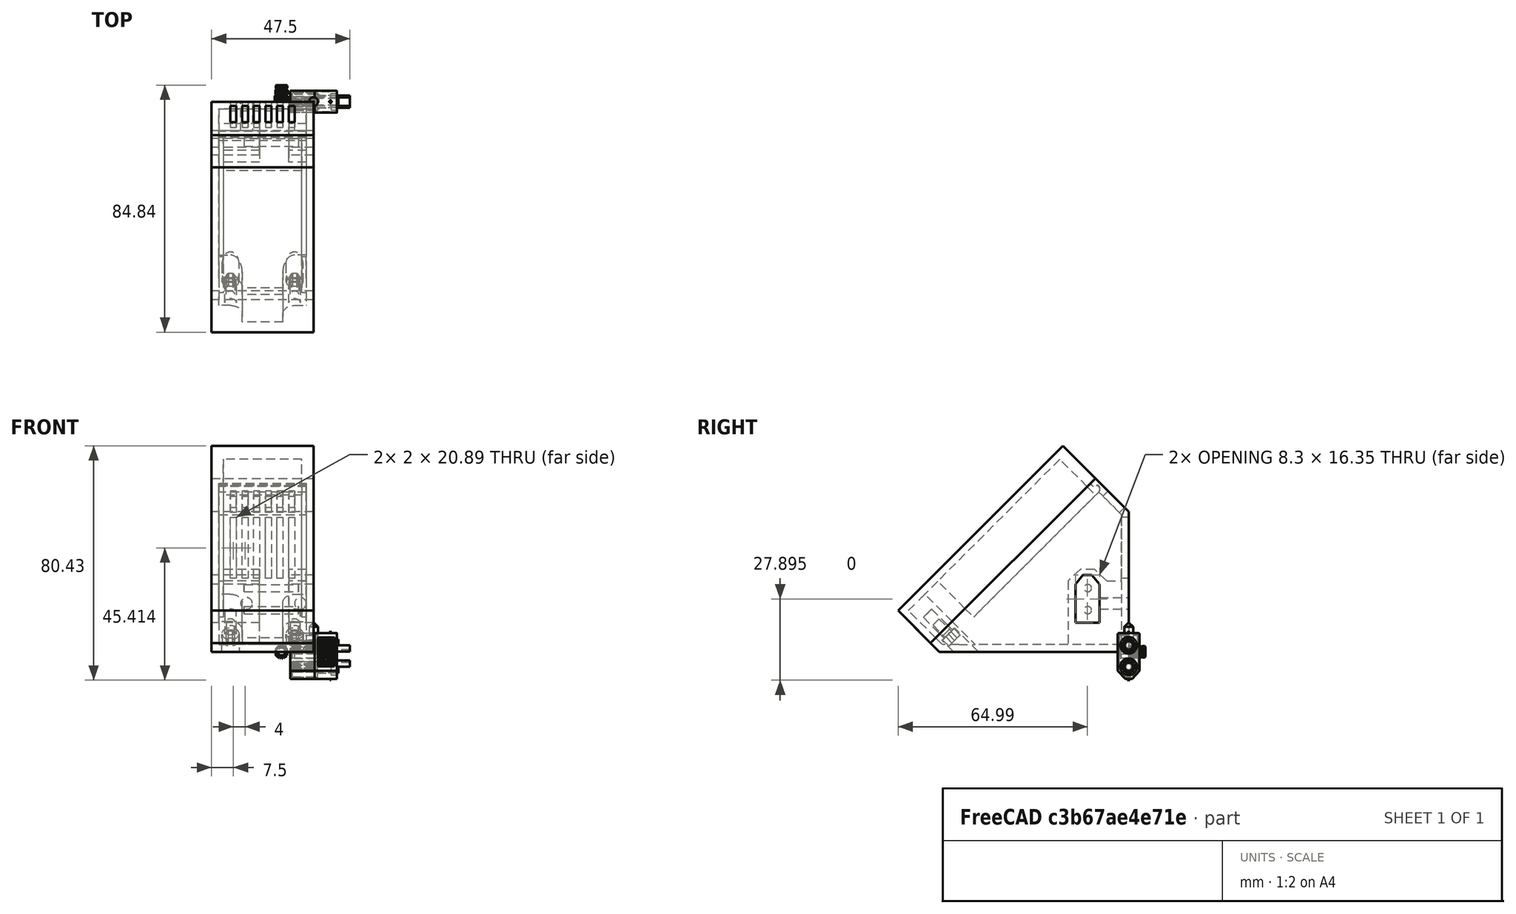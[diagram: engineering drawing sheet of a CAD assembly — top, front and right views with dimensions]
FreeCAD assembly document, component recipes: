
FREECAD ASSEMBLY — COMPONENT RECIPES ("alimMultiple_001_SurBase35mm_009.1")

This assembly document has 8 components, labeled P0..P7 below (a component is one placed body or linked part). 6 of them carry a construction recipe — the FreeCAD feature program that regenerates the part from scratch, quoted from this document or its linked companion documents; the rest are supplied as boundary geometry only. No exploded tour is included for this assembly.
COMPONENT P0 — recipe-attached ("base", modeled in this document).
Construction recipe (the document's own serialized feature program — sketch geometry with constraints, then the solid features built on it; lengths are millimeters unless a unit is written):

FEATURE [PartDesign::FeatureBase] Clone
  BaseFeature = -> Slice_child0
FEATURE [PartDesign::Thickness] Thickness
  Base = -> Clone [Face7]
  BaseFeature = -> Clone
  Intersection = false
  Join = 0
  Mode = 0
  Reversed = true
  SupportTransform = false
  Value = 2.5
  expr: Value = <<sp>>.epaisseurParois
FEATURE [PartDesign::Plane] DatumPlane001  label="planXt"
  AttachmentOffset = pos=(0,0,-2.5) rot=(0,0,1;0rad)
  Length = 110.737
  MapMode = 5
  Placement = pos=(-2.5,6e-16,-6e-16) rot=(0.57735,0.57735,0.57735;2.0944rad)
  ResizeMode = 0
  Support = -> [YZ_Plane002]
  Width = 102.305
  expr: .AttachmentOffset.Base.z = -<<sp>>.epaisseurParois
FEATURE [Sketcher::SketchObject] Sketch002  label="sk_renfortXt"
  FullyConstrained = true
  MapMode = 5
  Placement = pos=(-2.5,6e-16,-6e-16) rot=(0.57735,0.57735,0.57735;2.0944rad)
  Support = -> [DatumPlane001]
  expr: .Constraints.dist = <<sp>>.xt60distanceAngleBord
  expr: .Constraints.epRf = <<sp>>.xt60epRenfort
  expr: Constraints[13] = <<sp>>.xt60largeurFetiere
  expr: Constraints[14] = <<sp>>.xt60hauteur
  expr: Constraints[15] = <<sp>>.xt60hauteurToit
  expr: Constraints[16] = <<sp>>.xt60base
  expr: Constraints[18] = .Constraints.dist
  expr: Constraints[31] = <<sp>>.epaisseurParois
  expr: Constraints[32] = .Constraints.epRf
  expr: Constraints[34] = .Constraints.epRf
  expr: Constraints[45] = <<sp>>.epaisseurParois
  sketch-geometry (17):
    g0: LineSegment StartX=-18.3 StartY=10 StartZ=0 EndX=-18.3 EndY=23.25 EndZ=0
    g1: LineSegment StartX=-18.3 StartY=23.25 StartZ=0 EndX=-15.65 EndY=25.75 EndZ=0
    g2: LineSegment StartX=-15.65 StartY=25.75 StartZ=0 EndX=-12.65 EndY=25.75 EndZ=0
    g3: LineSegment StartX=-12.65 StartY=25.75 StartZ=0 EndX=-10 EndY=23.25 EndZ=0
    g4: LineSegment StartX=-10 StartY=23.25 StartZ=0 EndX=-10 EndY=10 EndZ=0
    g5: LineSegment StartX=-10 StartY=10 StartZ=0 EndX=-18.3 EndY=10 EndZ=0
    g6: LineSegment StartX=-14.15 StartY=10 StartZ=0 EndX=-14.15 EndY=25.75 EndZ=0
    g7: LineSegment StartX=-16.6431 StartY=28.25 StartZ=0 EndX=-20.8 EndY=24.3284 EndZ=0
    g8: LineSegment StartX=-20.8 StartY=24.3284 StartZ=0 EndX=-20.8 EndY=2.5 EndZ=0
    g9: LineSegment StartX=-20.8 StartY=2.5 StartZ=0 EndX=-7.5 EndY=2.5 EndZ=0
    g10: LineSegment StartX=-7.5 StartY=2.5 StartZ=0 EndX=-7.5 EndY=24.3284 EndZ=0
    g11: LineSegment StartX=-7.5 StartY=24.3284 StartZ=0 EndX=-11.6569 EndY=28.25 EndZ=0
    g12: LineSegment StartX=-11.6569 StartY=28.25 StartZ=0 EndX=-16.6431 EndY=28.25 EndZ=0
    g13: LineSegment StartX=-7.5 StartY=24.3284 StartZ=0 EndX=-2.5 EndY=24.3284 EndZ=0
    g14: LineSegment StartX=-2.5 StartY=24.3284 StartZ=0 EndX=-2.5 EndY=2.5 EndZ=0
    g15: LineSegment StartX=-2.5 StartY=2.5 StartZ=0 EndX=-7.5 EndY=2.5 EndZ=0
    g16: LineSegment StartX=-7.5 StartY=2.5 StartZ=0 EndX=-7.5 EndY=24.3284 EndZ=0
  constraints (46):
    c: Vertical(g0)
    c: Coincident(g0,g1)
    c: Coincident(g1,g2)
    c: Horizontal(g2)
    c: Coincident(g2,g3)
    c: Coincident(g3,g4)
    c: Vertical(g4)
    c: Coincident(g4,g5)
    c: Coincident(g5,g0)
    c: Horizontal(g5)
    c: Symmetric(g1,g2,g6)
    c: Equal(g0,g4)
    c: Symmetric(g0,g4,g6)
    c: DistanceX(g2,g2) = 3
    c: DistanceY(g4,g4) = 13.25
    c: DistanceY(g3,g2) = 2.5
    c: DistanceX(g5,g5) = 8.3
    c: DistanceX(g4,g-1) = 10  'dist'
    c: DistanceY(g-1,g4) = 10
    c: Coincident(g7,g8)
    c: Vertical(g8)
    c: Coincident(g8,g9)
    c: Horizontal(g9)
    c: Coincident(g9,g10)
    c: Coincident(g10,g11)
    c: Coincident(g11,g12)
    c: Coincident(g12,g7)
    c: Symmetric(g7,g10,g6)
    c: Symmetric(g7,g11,g6)
    c: Symmetric(g8,g9,g6)
    c: DistanceX(g8,g0) = 2.5  'epRf'
    c: DistanceY(g-1,g9) = 2.5
    c: Distance(g7,g1) = 2.5
    c: Parallel(g1,g7)
    c: DistanceY(g2,g11) = 2.5
    c: Coincident(g13,g14)
    c: Coincident(g14,g15)
    c: Coincident(g15,g16)
    c: Coincident(g16,g13)
    c: Horizontal(g13)
    c: Horizontal(g15)
    c: Vertical(g14)
    c: Vertical(g16)
    c: Coincident(g13,g11)
    c: Horizontal(g14,g9)
    c: DistanceX(g14,g-1) = 2.5
FEATURE [PartDesign::Pad] Pad001  label="renfortXt"
  AllowMultiFace = false
  BaseFeature = -> Thickness
  Direction = (1,1,1)
  Length = 30
  Length2 = 100
  Profile = -> Sketch002
  Reversed = true
  Type = 0
  expr: Length = <<sp>>.largeurModuleBase - 2 * <<sp>>.epaisseurParois
FEATURE [Sketcher::SketchObject] Sketch003  label="sk_trouXt"
  FullyConstrained = true
  MapMode = 5
  Placement = pos=(0,0,0) rot=(0.57735,0.57735,0.57735;2.0944rad)
  Support = -> [YZ_Plane002]
  expr: .Constraints.dist = <<sp>>.xt60distanceAngleBord
  expr: Constraints[13] = <<sp>>.xt60base
  expr: Constraints[14] = <<sp>>.xt60hauteur
  expr: Constraints[15] = <<sp>>.xt60hauteurToit + <<sp>>.xtJeu
  expr: Constraints[16] = <<sp>>.xt60largeurFetiere
  expr: Constraints[18] = .Constraints.dist
  sketch-geometry (7):
    g0: LineSegment StartX=-18.3 StartY=10 StartZ=0 EndX=-18.3 EndY=23.25 EndZ=0
    g1: LineSegment StartX=-18.3 StartY=23.25 StartZ=0 EndX=-15.65 EndY=26.35 EndZ=0
    g2: LineSegment StartX=-15.65 StartY=26.35 StartZ=0 EndX=-12.65 EndY=26.35 EndZ=0
    g3: LineSegment StartX=-12.65 StartY=26.35 StartZ=0 EndX=-10 EndY=23.25 EndZ=0
    g4: LineSegment StartX=-10 StartY=23.25 StartZ=0 EndX=-10 EndY=10 EndZ=0
    g5: LineSegment StartX=-10 StartY=10 StartZ=0 EndX=-18.3 EndY=10 EndZ=0
    g6: LineSegment StartX=-14.15 StartY=10 StartZ=0 EndX=-14.15 EndY=26.35 EndZ=0
  constraints (19):
    c: Vertical(g0)
    c: Coincident(g0,g1)
    c: Coincident(g1,g2)
    c: Horizontal(g2)
    c: Coincident(g2,g3)
    c: Coincident(g3,g4)
    c: Coincident(g4,g5)
    c: Coincident(g5,g0)
    c: Horizontal(g5)
    c: Symmetric(g1,g2,g6)
    c: Symmetric(g0,g3,g6)
    c: Vertical(g6)
    c: Symmetric(g0,g4,g6)
    c: DistanceX(g5,g5) = 8.3
    c: DistanceY(g4,g4) = 13.25
    c: DistanceY(g3,g2) = 3.1
    c: DistanceX(g2,g2) = 3
    c: DistanceX(g4,g-1) = 10  'dist'
    c: DistanceY(g-1,g4) = 10
FEATURE [PartDesign::Pocket] Pocket
  AllowMultiFace = false
  BaseFeature = -> Pad001
  Direction = (1,1,1)
  Length = 35
  Length2 = 100
  Profile = -> Sketch003
  Type = 0
  expr: Length = <<sp>>.largeurModuleBase
FEATURE [PartDesign::Plane] DatumPlane002  label="planDecoupeRenfortXt"
  AttachmentOffset = pos=(0,0,2.5) rot=(0,0,1;0rad)
  Length = 74.2466
  MapMode = 5
  Placement = pos=(0,-2.5,-6e-16) rot=(1,0,0;1.5708rad)
  ResizeMode = 0
  Support = -> [XZ_Plane002]
  Width = 98.8151
  expr: .AttachmentOffset.Base.z = <<sp>>.epaisseurParois
FEATURE [Sketcher::SketchObject] Sketch004  label="sk_decoupRenfXt"
  FullyConstrained = true
  MapMode = 5
  Placement = pos=(0,-2.5,-6e-16) rot=(1,0,0;1.5708rad)
  Support = -> [DatumPlane002]
  expr: Constraints[10] = <<sp>>.xt60LongueurRenfortPetit + <<sp>>.epaisseurParois
  expr: Constraints[11] = <<sp>>.largeurModuleBase - (<<sp>>.xt60longueurRenfortGrand + <<sp>>.epaisseurParois)
  expr: Constraints[8] = <<sp>>.epaisseurParois
  expr: Constraints[9] = <<sp>>.xt60distanceAngleBord + <<sp>>.xt60hauteur + <<sp>>.xt60hauteurToit + <<sp>>.xt60epRenfort
  sketch-geometry (4):
    g0: LineSegment StartX=-18.5 StartY=28.25 StartZ=0 EndX=-8.5 EndY=28.25 EndZ=0
    g1: LineSegment StartX=-8.5 StartY=28.25 StartZ=0 EndX=-8.5 EndY=2.5 EndZ=0
    g2: LineSegment StartX=-8.5 StartY=2.5 StartZ=0 EndX=-18.5 EndY=2.5 EndZ=0
    g3: LineSegment StartX=-18.5 StartY=2.5 StartZ=0 EndX=-18.5 EndY=28.25 EndZ=0
  constraints (12):
    c: Coincident(g0,g1)
    c: Coincident(g1,g2)
    c: Coincident(g2,g3)
    c: Coincident(g3,g0)
    c: Horizontal(g0)
    c: Horizontal(g2)
    c: Vertical(g1)
    c: Vertical(g3)
    c: DistanceY(g-1,g1) = 2.5
    c: DistanceY(g-1,g0) = 28.25
    c: DistanceX(g1,g-1) = 8.5
    c: DistanceX(g2,g-1) = 18.5
FEATURE [PartDesign::Pocket] Pocket001  label="decoupeRenfXt"
  AllowMultiFace = false
  BaseFeature = -> Pocket
  Direction = (1,1,1)
  Length = 23.3
  Length2 = 100
  Profile = -> Sketch004
  Reversed = true
  Type = 0
  expr: Length = <<sp>>.xt60distanceAngleBord + <<sp>>.xt60base + 2 * <<sp>>.xt60epRenfort
FEATURE [Sketcher::SketchObject] Sketch005  label="xt60PercagePostMale"
  FullyConstrained = true
  MapMode = 5
  Placement = pos=(0,0,0) rot=(1,0,0;1.5708rad)
  Support = -> [XZ_Plane002]
  expr: Constraints[0] = <<sp>>.insertDiamPercage
  expr: Constraints[1] = <<sp>>.insertDistanceTrouBordMale
  expr: Constraints[2] = <<sp>>.insertHauteur
  sketch-geometry (1):
    g0: Circle CenterX=-4.5 CenterY=16.625 CenterZ=0 NormalX=0 NormalY=0 NormalZ=1 AngleXU=0 Radius=2
  constraints (3):
    c: Diameter(g0) = 4
    c: DistanceX(g0,g-1) = 4.5
    c: DistanceY(g-1,g0) = 16.625
FEATURE [PartDesign::Pocket] Pocket002  label="insertXtMale"
  AllowMultiFace = false
  BaseFeature = -> Pocket001
  Direction = (1,1,1)
  Length = 10
  Length2 = 100
  Profile = -> Sketch005
  Reversed = true
  Type = 0
  expr: Length = <<sp>>.insertProfondeurPercage
FEATURE [Sketcher::SketchObject] Sketch006  label="xt60PercagePostFem"
  FullyConstrained = true
  MapMode = 5
  Placement = pos=(0,0,0) rot=(1,0,0;1.5708rad)
  Support = -> [XZ_Plane002]
  expr: Constraints[0] = <<sp>>.insertDiamPercage
  expr: Constraints[1] = <<sp>>.insertDistanceTrouBordFem
  expr: Constraints[2] = <<sp>>.insertHauteur
  sketch-geometry (1):
    g0: Circle CenterX=-23 CenterY=16.625 CenterZ=0 NormalX=0 NormalY=0 NormalZ=1 AngleXU=0 Radius=2
  constraints (3):
    c: Diameter(g0) = 4
    c: DistanceX(g0,g-1) = 23
    c: DistanceY(g-1,g0) = 16.625
FEATURE [PartDesign::Pocket] Pocket003  label="insertXt60Fem"
  AllowMultiFace = false
  BaseFeature = -> Pocket002
  Direction = (1,1,1)
  Length = 10
  Length2 = 100
  Profile = -> Sketch006
  Reversed = true
  Type = 0
  expr: Length = <<sp>>.insertProfondeurPercage
FEATURE [PartDesign::Plane] DatumPlane003
  AttachmentOffset = pos=(0,0,2.5) rot=(0,0,1;0rad)
  Length = 74.9399
  MapMode = 2
  Placement = pos=(0,0,2.5) rot=(0,0,1;0rad)
  ResizeMode = 0
  Support = -> [XY_Plane002]
  Width = 107.94
  expr: .AttachmentOffset.Base.z = <<sp>>.epaisseurParois
FEATURE [PartDesign::Plane] DatumPlane004  label="planTrancheur"
  AttachmentOffset = pos=(0,0,71) rot=(-1,0,0;0.785398rad)
  Length = 77.3593
  MapMode = 5
  Placement = pos=(0,-71,-1.58e-14) rot=(1,0,0;0.785398rad)
  ResizeMode = 0
  Support = -> [XZ_Plane002]
  Width = 142.919
  expr: .AttachmentOffset.Base.z = <<sp>>.planTrancheur
FEATURE [Sketcher::SketchObject] Sketch008
  FullyConstrained = true
  MapMode = 5
  Placement = pos=(0,-71,-2.13e-14) rot=(1,0,0;0.785398rad)
  Support = -> [DatumPlane004]
  expr: .Constraints.dist = <<sp>>.epaisseurParois
  expr: Constraints[13] = <<sp>>.epaisseurParois
  expr: Constraints[16] = <<sp>>.insertDiamPercage / 2 + <<sp>>.insertFAVMargeDist
  expr: Constraints[1] = <<sp>>.insertFavDistAuZeroDuPLan
  expr: Constraints[21] = <<sp>>.insertFAVDistBord
  expr: Constraints[22] = <<sp>>.largeurModuleBase - <<sp>>.epaisseurParois
  sketch-geometry (7):
    g0: LineSegment StartX=-2.5 StartY=4.24264 StartZ=0 EndX=-32.5 EndY=4.24264 EndZ=0
    g1: LineSegment StartX=-6.5 StartY=14.7426 StartZ=0 EndX=-2.5 EndY=14.7426 EndZ=0
    g2: LineSegment StartX=-2.5 StartY=14.7426 StartZ=0 EndX=-2.5 EndY=6.74264 EndZ=0
    g3: LineSegment StartX=-2.5 StartY=6.74264 StartZ=0 EndX=-10.5 EndY=6.74264 EndZ=0
    g4: LineSegment StartX=-10.5 StartY=6.74264 StartZ=0 EndX=-10.5 EndY=10.7426 EndZ=0
    g5: ArcOfCircle CenterX=-6.5 CenterY=10.7426 CenterZ=0 NormalX=0 NormalY=0 NormalZ=1 AngleXU=0 Radius=4 StartAngle=1.5708 EndAngle=3.14159
    g6: LineSegment StartX=-6.5 StartY=10.7426 StartZ=0 EndX=-6.5 EndY=6.74264 EndZ=0
  constraints (23):
    c: Horizontal(g0)
    c: DistanceY(g-1,g0) = 4.24264
    c: DistanceX(g0,g-1) = 2.5  'dist'
    c: Horizontal(g1)
    c: Coincident(g1,g2)
    c: Vertical(g2)
    c: Coincident(g2,g3)
    c: Horizontal(g3)
    c: Coincident(g3,g4)
    c: Vertical(g4)
    c: Vertical(g2,g0)
    c: Equal(g3,g2)
    c: Equal(g4,g1)
    c: DistanceY(g0,g2) = 2.5
    c: Coincident(g5,g4)
    c: Coincident(g5,g1)
    c: DistanceX(g5,g2) = 4
    c: Coincident(g6,g5)
    c: PointOnObject(g6,g3)
    c: Vertical(g6)
    c: Vertical(g5,g1)
    c: DistanceX(g3,g3) = 8
    c: DistanceX(g0,g-1) = 32.5
FEATURE [PartDesign::Pad] Pad003  label="padTrouFAVDroite"
  AllowMultiFace = false
  BaseFeature = -> Pocket003
  Direction = (1,1,1)
  Length = 10
  Length2 = 100
  Profile = -> Sketch008
  Reversed = true
  Type = 3
  UpToFace = -> DatumPlane003
FEATURE [Sketcher::SketchObject] Sketch009
  FullyConstrained = true
  MapMode = 5
  Placement = pos=(0,-71,-2.13e-14) rot=(1,0,0;0.785398rad)
  Support = -> [DatumPlane004]
  expr: .Constraints.larg = <<sp>>.insertFAVDistBord
  expr: Constraints[11] = .Constraints.larg / 2
  expr: Constraints[12] = <<sp>>.largeurModuleBase
  expr: Constraints[13] = <<sp>>.insertFavDistAuZeroDuPLan
  expr: Constraints[14] = <<sp>>.epaisseurParois
  expr: Constraints[15] = <<sp>>.epaisseurParois
  expr: Constraints[8] = .Constraints.larg
  sketch-geometry (6):
    g0: LineSegment StartX=-32.5 StartY=6.74264 StartZ=0 EndX=-24.5 EndY=6.74264 EndZ=0
    g1: LineSegment StartX=-24.5 StartY=6.74264 StartZ=0 EndX=-24.5 EndY=10.7426 EndZ=0
    g2: LineSegment StartX=-28.5 StartY=14.7426 StartZ=0 EndX=-32.5 EndY=14.7426 EndZ=0
    g3: LineSegment StartX=-32.5 StartY=14.7426 StartZ=0 EndX=-32.5 EndY=6.74264 EndZ=0
    g4: ArcOfCircle CenterX=-28.5 CenterY=10.7426 CenterZ=0 NormalX=0 NormalY=0 NormalZ=1 AngleXU=0 Radius=4 StartAngle=2e-16 EndAngle=1.5708
    g5: GeomPoint X=-35 Y=4.24264 Z=0
  constraints (16):
    c: Coincident(g0,g1)
    c: Coincident(g2,g3)
    c: Coincident(g3,g0)
    c: Horizontal(g0)
    c: Horizontal(g2)
    c: Vertical(g1)
    c: Vertical(g3)
    c: DistanceX(g0,g0) = 8  'larg'
    c: DistanceY(g3,g3) = 8
    c: Tangent(g2,g4) = -1.5708
    c: Tangent(g1,g4) = -1.5708
    c: DistanceX(g0,g4) = 4
    c: DistanceX(g5,g-1) = 35
    c: DistanceY(g-1,g5) = 4.24264
    c: DistanceX(g5,g0) = 2.5
    c: DistanceY(g5,g0) = 2.5
FEATURE [PartDesign::Pad] Pad004  label="padTrouFavGauche"
  AllowMultiFace = false
  BaseFeature = -> Pad003
  Direction = (1,1,1)
  Length = 10
  Length2 = 100
  Profile = -> Sketch009
  Type = 3
  UpToFace = -> DatumPlane003 [Plane]
FEATURE [Sketcher::SketchObject] Sketch010
  FullyConstrained = true
  MapMode = 5
  Placement = pos=(0,-71,-2.13e-14) rot=(1,0,0;0.785398rad)
  Support = -> [DatumPlane004]
  expr: Constraints[0] = <<sp>>.insertFAVDistBord / 2 + <<sp>>.epaisseurParois
  expr: Constraints[1] = <<sp>>.insertFavDistAuZeroDuPLan + <<sp>>.epaisseurParois + <<sp>>.insertFAVDistBord / 2
  expr: Constraints[2] = <<sp>>.insertDiamPercage
  sketch-geometry (1):
    g0: Circle CenterX=-6.5 CenterY=10.7426 CenterZ=0 NormalX=0 NormalY=0 NormalZ=1 AngleXU=0 Radius=2
  constraints (3):
    c: DistanceX(g0,g-1) = 6.5
    c: DistanceY(g-1,g0) = 10.7426
    c: Diameter(g0) = 4
FEATURE [PartDesign::Pocket] Pocket004  label="trouDroit"
  AllowMultiFace = false
  BaseFeature = -> Pad004
  Direction = (1,1,1)
  Length = 5
  Length2 = 100
  Profile = -> Sketch010
  Type = 1
FEATURE [Sketcher::SketchObject] Sketch011
  FullyConstrained = true
  MapMode = 5
  Placement = pos=(0,-71,-2.13e-14) rot=(1,0,0;0.785398rad)
  Support = -> [DatumPlane004]
  expr: Constraints[0] = <<sp>>.insertDiamPercage
  expr: Constraints[1] = <<sp>>.largeurModuleBase - <<sp>>.epaisseurParois - <<sp>>.insertFAVDistBord / 2
  expr: Constraints[2] = <<sp>>.insertFavDistAuZeroDuPLan + <<sp>>.epaisseurParois + <<sp>>.insertFAVDistBord / 2
  sketch-geometry (1):
    g0: Circle CenterX=-28.5 CenterY=10.7426 CenterZ=0 NormalX=0 NormalY=0 NormalZ=1 AngleXU=0 Radius=2
  constraints (3):
    c: Diameter(g0) = 4
    c: DistanceX(g0,g-1) = 28.5
    c: DistanceY(g-1,g0) = 10.7426
FEATURE [PartDesign::Pocket] Pocket005  label="trouGauche"
  AllowMultiFace = false
  BaseFeature = -> Pocket004
  Direction = (1,1,1)
  Length = 5
  Length2 = 100
  Profile = -> Sketch011
  Type = 1
FEATURE [PartDesign::Plane] DatumPlane005  label="planTeteVisFav"
  AttachmentOffset = pos=(0,0,68) rot=(-1,0,0;0.785398rad)
  Length = 77.3593
  MapMode = 5
  Placement = pos=(0,-68,-1.51e-14) rot=(1,0,0;0.785398rad)
  ResizeMode = 0
  Support = -> [XZ_Plane002]
  Width = 142.919
  expr: .AttachmentOffset.Base.z = <<sp>>.planTrancheur - 3
FEATURE [Sketcher::SketchObject] Sketch012
  ExternalGeometry = -> [Pocket005]
  FullyConstrained = true
  MapMode = 5
  Placement = pos=(0,-68,-1.42e-14) rot=(1,0,0;0.785398rad)
  Support = -> [DatumPlane005]
  expr: Constraints[1] = <<sp>>.visM3DiamEncastrement
  sketch-geometry (2):
    g0: Circle CenterX=-6.5 CenterY=8.62132 CenterZ=0 NormalX=0 NormalY=0 NormalZ=1 AngleXU=0 Radius=3
    g1: Circle CenterX=-28.5 CenterY=8.62132 CenterZ=0 NormalX=0 NormalY=0 NormalZ=1 AngleXU=0 Radius=3
  constraints (4):
    c: Equal(g0,g1)
    c: Diameter(g1) = 6
    c: Coincident(g1,g-4)
    c: Coincident(g-3,g0)
FEATURE [PartDesign::Pocket] Pocket006  label="evidementTeteVisFav"
  AllowMultiFace = false
  BaseFeature = -> Pocket005
  Direction = (1,1,1)
  Length = 20
  Length2 = 100
  Profile = -> Sketch012
  Type = 1
FEATURE [Sketcher::SketchObject] Sketch014
  FullyConstrained = true
  MapMode = 5
  Placement = pos=(0,0,0) rot=(1,0,0;1.5708rad)
  Support = -> [XZ_Plane002]
  expr: Constraints[12] = <<sp>>.xt60distanceAngleBord + <<sp>>.xt60hauteur + <<sp>>.ventilDistBordFente
  expr: Constraints[13] = <<sp>>.ventilLargeurFentes
  expr: Constraints[14] = <<sp>>.ventilEcartfente / 2
  expr: Constraints[15] = <<sp>>.hauteurDuDos - <<sp>>.ventilDistBordFente
  expr: Constraints[2] = <<sp>>.hauteurDuDos
  expr: Constraints[3] = <<sp>>.largeurModuleBase / 2
  sketch-geometry (5):
    g0: LineSegment StartX=-17.5 StartY=0 StartZ=0 EndX=-17.5 EndY=48.1371 EndZ=0
    g1: LineSegment StartX=-20.5 StartY=46.1371 StartZ=0 EndX=-18.5 EndY=46.1371 EndZ=0
    g2: LineSegment StartX=-18.5 StartY=46.1371 StartZ=0 EndX=-18.5 EndY=25.25 EndZ=0
    g3: LineSegment StartX=-18.5 StartY=25.25 StartZ=0 EndX=-20.5 EndY=25.25 EndZ=0
    g4: LineSegment StartX=-20.5 StartY=25.25 StartZ=0 EndX=-20.5 EndY=46.1371 EndZ=0
  constraints (16):
    c: PointOnObject(g0,g-1)
    c: Vertical(g0)
    c: DistanceY(g0,g0) = 48.1371
    c: DistanceX(g0,g-1) = 17.5
    c: Coincident(g1,g2)
    c: Coincident(g2,g3)
    c: Coincident(g3,g4)
    c: Coincident(g4,g1)
    c: Horizontal(g1)
    c: Horizontal(g3)
    c: Vertical(g2)
    c: Vertical(g4)
    c: DistanceY(g-1,g2) = 25.25
    c: DistanceX(g1,g1) = 2
    c: DistanceX(g2,g0) = 1
    c: DistanceY(g-1,g1) = 46.1371
FEATURE [PartDesign::Pocket] Pocket008  label="ventilFente1"
  AllowMultiFace = false
  BaseFeature = -> Pocket006
  Direction = (1,1,1)
  Length = 2.5
  Length2 = 100
  Profile = -> Sketch014
  Reversed = true
  Type = 0
  expr: Length = <<sp>>.epaisseurParois
FEATURE [PartDesign::LinearPattern] LinearPattern  label="ventilDosRepeat1"
  BaseFeature = -> Pocket008
  Direction = -> Sketch014 [H_Axis]
  Length = 8
  Occurrences = 3
  Originals = -> [Pocket008]
  Reversed = true
  expr: Length = <<sp>>.ventilLargeurRepet
  expr: Occurrences = <<sp>>.ventilNbrFents
FEATURE [PartDesign::LinearPattern] LinearPattern001  label="ventilDosRepeat2"
  BaseFeature = -> LinearPattern
  Direction = -> Sketch014 [H_Axis]
  Length = 12
  Occurrences = 4
  Originals = -> [Pocket008]
  expr: Length = <<sp>>.ventilLargeurRepet + <<sp>>.ventilEcartfente + <<sp>>.ventilLargeurFentes
  expr: Occurrences = <<sp>>.ventilNbrFents + 1
FEATURE [PartDesign::Plane] DatumPlane006  label="planVentilSup"
  AttachmentOffset = pos=(0,0,-48.1371) rot=(1,0,0;0.785398rad)
  Length = 77.3593
  MapMode = 5
  Placement = pos=(0,48.1371,1.07e-14) rot=(1,0,0;2.35619rad)
  ResizeMode = 0
  Support = -> [XZ_Plane002]
  Width = 142.919
  expr: .AttachmentOffset.Base.z = -<<sp>>.hauteurDuDos
FEATURE [Sketcher::SketchObject] Sketch015
  FullyConstrained = true
  MapMode = 5
  Placement = pos=(0,48.1371,1.07e-14) rot=(1,0,0;2.35619rad)
  Support = -> [DatumPlane006]
  expr: Constraints[10] = <<sp>>.ventilLargeurFentes
  expr: Constraints[11] = (<<sp>>.largeurModuleBase + <<sp>>.ventilEcartfente) / 2
  expr: Constraints[8] = <<sp>>.distanceAuZeroPlanBorArriere + <<sp>>.ventilDistBordFente
  expr: Constraints[9] = <<sp>>.longPetitRetSupSansFav - 2 * <<sp>>.ventilDistBordFente - <<sp>>.favBordureProf
  sketch-geometry (4):
    g0: LineSegment StartX=-18.5 StartY=78.0926 StartZ=0 EndX=-20.5 EndY=78.0926 EndZ=0
    g1: LineSegment StartX=-20.5 StartY=78.0926 StartZ=0 EndX=-20.5 EndY=70.0761 EndZ=0
    g2: LineSegment StartX=-20.5 StartY=70.0761 StartZ=0 EndX=-18.5 EndY=70.0761 EndZ=0
    g3: LineSegment StartX=-18.5 StartY=70.0761 StartZ=0 EndX=-18.5 EndY=78.0926 EndZ=0
  constraints (12):
    c: Coincident(g0,g1)
    c: Coincident(g1,g2)
    c: Coincident(g2,g3)
    c: Coincident(g3,g0)
    c: Horizontal(g0)
    c: Horizontal(g2)
    c: Vertical(g1)
    c: Vertical(g3)
    c: DistanceY(g-1,g2) = 70.0761
    c: DistanceY(g2,g0) = 8.01652
    c: DistanceX(g0,g0) = 2
    c: DistanceX(g2,g-1) = 18.5
FEATURE [PartDesign::Pocket] Pocket009  label="ventilSupFente"
  AllowMultiFace = false
  BaseFeature = -> LinearPattern001
  Direction = (1,1,1)
  Length = 5
  Length2 = 100
  Profile = -> Sketch015
  Reversed = true
  Type = 0
FEATURE [PartDesign::LinearPattern] LinearPattern002  label="ventilSupRepeat1"
  BaseFeature = -> Pocket009
  Direction = -> Sketch015 [H_Axis]
  Length = 8
  Occurrences = 3
  Originals = -> [Pocket009]
  Reversed = true
  expr: Length = <<sp>>.ventilLargeurRepet
  expr: Occurrences = <<sp>>.ventilNbrFents
FEATURE [PartDesign::LinearPattern] LinearPattern003  label="ventilSupRepeat2"
  BaseFeature = -> LinearPattern002
  Direction = -> Sketch015 [H_Axis]
  Length = 12
  Occurrences = 4
  Originals = -> [Pocket009]
  expr: Length = <<sp>>.ventilLargeurRepet + <<sp>>.ventilEcartfente + <<sp>>.ventilLargeurFentes
  expr: Occurrences = <<sp>>.ventilNbrFents + 1
FEATURE [PartDesign::Body] Body001  label="base"
  BaseFeature = -> Slice_child0
  Group = -> [Clone,Thickness,DatumPlane001,Sketch002,Pad001,Sketch003,Pocket,DatumPlane002,Sketch004,Pocket001,Sketch005,Pocket002,Sketch006,Pocket003,DatumPlane003,DatumPlane004,Sketch008,Pad003,Sketch009,Pad004,Sketch010,Pocket004,Sketch011,Pocket005,DatumPlane005,Sketch012,Pocket006,Sketch014,Pocket008,LinearPattern,LinearPattern001,DatumPlane006,Sketch015,Pocket009,LinearPattern002,LinearPattern003,+3 more]
  Origin = -> Origin002
  Tip = -> Pocket015
COMPONENT P1 — recipe-attached ("faceAvant", modeled in this document).
Construction recipe (the document's own serialized feature program — sketch geometry with constraints, then the solid features built on it; lengths are millimeters unless a unit is written):

FEATURE [PartDesign::FeatureBase] Clone001
  BaseFeature = -> Slice_child1
FEATURE [PartDesign::Thickness] Thickness001
  Base = -> Clone001 [Face5]
  BaseFeature = -> Clone001
  Intersection = false
  Join = 0
  Mode = 0
  Reversed = true
  SupportTransform = false
  Value = 2.5
  expr: Value = <<sp>>.epaisseurParois
FEATURE [PartDesign::Plane] DatumPlane007  label="planTrancheurBis"
  AttachmentOffset = pos=(0,0,71) rot=(-1,0,0;0.785398rad)
  Length = 78.4163
  MapMode = 5
  Placement = pos=(0,-71,-1.58e-14) rot=(1,0,0;0.785398rad)
  ResizeMode = 0
  Support = -> [XZ_Plane003]
  Width = 159.734
  expr: .AttachmentOffset.Base.z = <<sp>>.planTrancheur
FEATURE [Sketcher::SketchObject] Sketch016  label="sk_insertFavDroit"
  FullyConstrained = true
  MapMode = 5
  Placement = pos=(0,-71,-2.13e-14) rot=(1,0,0;0.785398rad)
  Support = -> [DatumPlane007]
  expr: Constraints[11] = <<sp>>.insertFAVDistBord
  expr: Constraints[14] = <<sp>>.insertFAVDistBord / 2
  expr: Constraints[7] = <<sp>>.epaisseurParois
  expr: Constraints[8] = <<sp>>.insertFavDistAuZeroDuPLan + <<sp>>.epaisseurParois
  expr: Constraints[9] = <<sp>>.insertFAVDistBord
  sketch-geometry (5):
    g0: LineSegment StartX=-6.5 StartY=14.7426 StartZ=0 EndX=-2.5 EndY=14.7426 EndZ=0
    g1: LineSegment StartX=-2.5 StartY=14.7426 StartZ=0 EndX=-2.5 EndY=6.74264 EndZ=0
    g2: LineSegment StartX=-2.5 StartY=6.74264 StartZ=0 EndX=-10.5 EndY=6.74264 EndZ=0
    g3: LineSegment StartX=-10.5 StartY=6.74264 StartZ=0 EndX=-10.5 EndY=10.7426 EndZ=0
    g4: ArcOfCircle CenterX=-6.5 CenterY=10.7426 CenterZ=0 NormalX=0 NormalY=0 NormalZ=1 AngleXU=0 Radius=4 StartAngle=1.5708 EndAngle=3.14159
  constraints (15):
    c: Horizontal(g0)
    c: Coincident(g0,g1)
    c: Vertical(g1)
    c: Coincident(g1,g2)
    c: Horizontal(g2)
    c: Coincident(g2,g3)
    c: Vertical(g3)
    c: DistanceX(g1,g-1) = 2.5
    c: DistanceY(g-1,g1) = 6.74264
    c: DistanceY(g1,g1) = 8
    c: Equal(g3,g0)
    c: DistanceX(g2,g2) = 8
    c: Coincident(g4,g0)
    c: Tangent(g4,g3) = 1.5708
    c: DistanceX(g4,g1) = 4
FEATURE [PartDesign::Pad] Pad005  label="padInsertFavDroit"
  AllowMultiFace = false
  BaseFeature = -> Thickness001
  Direction = (1,1,1)
  Length = 10
  Length2 = 100
  Profile = -> Sketch016
  Type = 2
FEATURE [Sketcher::SketchObject] Sketch017  label="sp_padInserFavGauch"
  FullyConstrained = true
  MapMode = 5
  Placement = pos=(0,-71,-2.13e-14) rot=(1,0,0;0.785398rad)
  Support = -> [DatumPlane007]
  expr: Constraints[10] = <<sp>>.insertFAVDistBord
  expr: Constraints[12] = <<sp>>.insertFAVDistBord / 2
  expr: Constraints[13] = <<sp>>.largeurModuleBase
  expr: Constraints[14] = <<sp>>.insertFavDistAuZeroDuPLan
  expr: Constraints[15] = <<sp>>.epaisseurParois
  expr: Constraints[16] = <<sp>>.epaisseurParois
  sketch-geometry (6):
    g0: LineSegment StartX=-28.5 StartY=14.7426 StartZ=0 EndX=-32.5 EndY=14.7426 EndZ=0
    g1: LineSegment StartX=-32.5 StartY=14.7426 StartZ=0 EndX=-32.5 EndY=6.74264 EndZ=0
    g2: LineSegment StartX=-32.5 StartY=6.74264 StartZ=0 EndX=-24.5 EndY=6.74264 EndZ=0
    g3: LineSegment StartX=-24.5 StartY=6.74264 StartZ=0 EndX=-24.5 EndY=10.7426 EndZ=0
    g4: ArcOfCircle CenterX=-28.5 CenterY=10.7426 CenterZ=0 NormalX=0 NormalY=0 NormalZ=1 AngleXU=0 Radius=4 StartAngle=8.70802e-11 EndAngle=1.5708
    g5: GeomPoint X=-35 Y=4.24264 Z=0
  constraints (17):
    c: Horizontal(g0)
    c: Coincident(g0,g1)
    c: Vertical(g1)
    c: Coincident(g1,g2)
    c: Horizontal(g2)
    c: Coincident(g2,g3)
    c: Vertical(g3)
    c: Equal(g3,g0)
    c: Equal(g2,g1)
    c: Coincident(g0,g4)
    c: DistanceX(g2,g2) = 8
    c: Tangent(g4,g3) = -1.5708
    c: DistanceX(g0,g0) = 4
    c: DistanceX(g5,g-1) = 35
    c: DistanceY(g-1,g5) = 4.24264
    c: DistanceY(g5,g1) = 2.5
    c: DistanceX(g5,g1) = 2.5
FEATURE [PartDesign::Pad] Pad006  label="padInsertFavGauch"
  AllowMultiFace = false
  BaseFeature = -> Pad005
  Direction = (1,1,1)
  Length = 10
  Length2 = 100
  Profile = -> Sketch017
  Type = 2
FEATURE [Sketcher::SketchObject] Sketch018  label="skPercageInsertFavDroit"
  FullyConstrained = true
  MapMode = 5
  Placement = pos=(0,-71,-2.13e-14) rot=(1,0,0;0.785398rad)
  Support = -> [DatumPlane007]
  expr: Constraints[0] = <<sp>>.insertDiamPercage
  expr: Constraints[1] = <<sp>>.insertFavDistAuZeroDuPLan + <<sp>>.epaisseurParois + <<sp>>.insertFAVDistBord / 2
  expr: Constraints[2] = <<sp>>.epaisseurParois + <<sp>>.insertFAVDistBord / 2
  expr: Constraints[7] = <<sp>>.largeurModuleBase - 2 * <<sp>>.epaisseurParois - <<sp>>.insertFAVDistBord
  sketch-geometry (3):
    g0: Circle CenterX=-6.5 CenterY=10.7426 CenterZ=0 NormalX=0 NormalY=0 NormalZ=1 AngleXU=0 Radius=2
    g1: Circle CenterX=-28.5 CenterY=10.7426 CenterZ=0 NormalX=0 NormalY=0 NormalZ=1 AngleXU=0 Radius=2
    g2: LineSegment StartX=-28.5 StartY=10.7426 StartZ=0 EndX=-6.5 EndY=10.7426 EndZ=0
  constraints (8):
    c: Diameter(g0) = 4
    c: DistanceY(g-1,g0) = 10.7426
    c: DistanceX(g0,g-1) = 6.5
    c: Equal(g0,g1)
    c: Coincident(g2,g1)
    c: Coincident(g2,g0)
    c: Horizontal(g2)
    c: DistanceX(g2,g2) = 22
FEATURE [PartDesign::Pocket] Pocket010  label="trouInsertFavDroit"
  AllowMultiFace = false
  BaseFeature = -> Pad006
  Direction = (1,1,1)
  Length = 8
  Length2 = 100
  Profile = -> Sketch018
  Reversed = true
  Type = 0
  expr: Length = <<sp>>.insertFavProfondeur
FEATURE [PartDesign::Plane] DatumPlane011  label="planFaceAvant"
  AttachmentOffset = pos=(0,0,93.2843) rot=(-1,0,0;0.785398rad)
  Length = 78.4163
  MapMode = 5
  Placement = pos=(0,-93.2843,-2.07e-14) rot=(1,0,0;0.785398rad)
  ResizeMode = 0
  Support = -> [XZ_Plane003]
  Width = 159.734
  expr: .AttachmentOffset.Base.z = <<sp>>.planFaceAvant
FEATURE [Sketcher::SketchObject] Sketch030  label="sk_rebordFav"
  FullyConstrained = true
  MapMode = 5
  Placement = pos=(0,-71,-2.13e-14) rot=(1,0,0;0.785398rad)
  Support = -> [DatumPlane007]
  expr: Constraints[0] = <<sp>>.insertFavDistAuZeroDuPLan
  expr: Constraints[19] = <<sp>>.epaisseurParois
  expr: Constraints[20] = <<sp>>.favEpBordure
  expr: Constraints[21] = <<sp>>.favDistBordPlan
  expr: Constraints[22] = <<sp>>.largeurModuleBase - 2 * <<sp>>.epaisseurParois
  expr: Constraints[23] = <<sp>>.favEpBordure
  expr: Constraints[24] = <<sp>>.Face - <<sp>>.epaisseurParois
  expr: Constraints[25] = <<sp>>.favEpBordure
  sketch-geometry (9):
    g0: GeomPoint X=0 Y=4.24264 Z=0
    g1: LineSegment StartX=-32.5 StartY=20.9853 StartZ=0 EndX=-32.5 EndY=81.7426 EndZ=0
    g2: LineSegment StartX=-32.5 StartY=81.7426 StartZ=0 EndX=-2.5 EndY=81.7426 EndZ=0
    g3: LineSegment StartX=-2.5 StartY=81.7426 StartZ=0 EndX=-2.5 EndY=20.9853 EndZ=0
    g4: LineSegment StartX=-2.5 StartY=20.9853 StartZ=0 EndX=-4 EndY=20.9853 EndZ=0
    g5: LineSegment StartX=-4 StartY=20.9853 StartZ=0 EndX=-4 EndY=80.2426 EndZ=0
    g6: LineSegment StartX=-4 StartY=80.2426 StartZ=0 EndX=-31 EndY=80.2426 EndZ=0
    g7: LineSegment StartX=-31 StartY=80.2426 StartZ=0 EndX=-31 EndY=20.9853 EndZ=0
    g8: LineSegment StartX=-31 StartY=20.9853 StartZ=0 EndX=-32.5 EndY=20.9853 EndZ=0
  constraints (26):
    c: DistanceY(g-1,g0) = 4.24264
    c: Vertical(g0,g-1)
    c: Vertical(g1)
    c: Coincident(g1,g2)
    c: Horizontal(g2)
    c: Coincident(g2,g3)
    c: Vertical(g3)
    c: Coincident(g3,g4)
    c: Horizontal(g4)
    c: Coincident(g4,g5)
    c: Vertical(g5)
    c: Coincident(g5,g6)
    c: Horizontal(g6)
    c: Coincident(g6,g7)
    c: Vertical(g7)
    c: Coincident(g7,g8)
    c: Coincident(g8,g1)
    c: Horizontal(g8)
    c: Horizontal(g7,g4)
    c: DistanceX(g3,g0) = 2.5
    c: DistanceX(g4,g4) = 1.5
    c: DistanceY(g0,g3) = 16.7426
    c: DistanceX(g1,g3) = 30
    c: DistanceY(g5,g2) = 1.5
    c: DistanceY(g0,g2) = 77.5
    c: DistanceX(g1,g7) = 1.5
FEATURE [PartDesign::Pad] Pad014  label="favRebordSupport"
  AllowMultiFace = false
  BaseFeature = -> Pocket010
  Direction = (1,1,1)
  Length = 10
  Length2 = 100
  Profile = -> Sketch030
  Type = 3
  UpToFace = -> Pocket010 [Face13]
FEATURE [PartDesign::Pad] Pad015  label="favRebord"
  AllowMultiFace = false
  BaseFeature = -> Pad014
  Direction = (1,1,1)
  Length = 4.15
  Length2 = 100
  Profile = -> Sketch030
  Reversed = true
  Type = 0
  expr: Length = <<sp>>.favBordureProf
FEATURE [Sketcher::SketchObject] Sketch031  label="sk_bourlet"
  ExternalGeometry = -> [Pad015]
  FullyConstrained = true
  MapMode = 5
  Placement = pos=(-2.5,0,0) rot=(0.57735,0.57735,0.57735;2.0944rad)
  Support = -> [Pad015]
  expr: Constraints[3] = <<sp>>.bourletMaintientRayon - <<sp>>.bourletRayonJeu
  sketch-geometry (2):
    g0: ArcOfCircle CenterX=-11.184 CenterY=55.7855 CenterZ=0 NormalX=0 NormalY=0 NormalZ=1 AngleXU=0 Radius=1.3 StartAngle=5.49779 EndAngle=8.63938
    g1: LineSegment StartX=-12.1032 StartY=56.7048 StartZ=0 EndX=-10.2647 EndY=54.8663 EndZ=0
  constraints (6):
    c: Coincident(g0,g-3)
    c: PointOnObject(g0,g-3)
    c: PointOnObject(g0,g-3)
    c: Radius(g0) = 1.3
    c: Coincident(g1,g0)
    c: Coincident(g1,g0)
FEATURE [PartDesign::Pad] Pad016  label="bourlet"
  AllowMultiFace = false
  BaseFeature = -> Pad015
  Direction = (1,1,1)
  Length = 10
  Length2 = 100
  Profile = -> Sketch031
  Reversed = true
  Type = 3
  UpToFace = -> Pad015 [Face11]
FEATURE [PartDesign::Body] Body002  label="faceAvant"
  BaseFeature = -> Slice_child1
  Group = -> [Clone001,Thickness001,DatumPlane007,Sketch016,Pad005,Sketch017,Pad006,Sketch018,Pocket010,DatumPlane011,Sketch030,Pad014,Pad015,Sketch031,Pad016]
  Origin = -> Origin003
  Tip = -> Pad016
COMPONENT P2 — recipe-attached ("potar", modeled in this document).
Construction recipe (the document's own serialized feature program — sketch geometry with constraints, then the solid features built on it; lengths are millimeters unless a unit is written):

FEATURE [Sketcher::SketchObject] Sketch  label="profileDeBase"
  FullyConstrained = true
  MapMode = 5
  Placement = pos=(0,0,0) rot=(0.57735,0.57735,0.57735;2.0944rad)
  Support = -> [YZ_Plane001]
  expr: Constraints[10] = <<sp>>.petitRetour
  expr: Constraints[11] = <<sp>>.angleFacePetitRetour
  expr: Constraints[12] = <<sp>>.Face
  expr: Constraints[13] = <<sp>>.angleFaceRetourHaut
  expr: Constraints[8] = <<sp>>.Base
  expr: Constraints[9] = <<sp>>.anglePetitRetourBase
  sketch-geometry (5):
    g0: LineSegment StartX=0 StartY=0 StartZ=0 EndX=-65 EndY=0 EndZ=0
    g1: LineSegment StartX=-65 StartY=0 StartZ=0 EndX=-79.1421 EndY=14.1421 EndZ=0
    g2: LineSegment StartX=-79.1421 StartY=14.1421 StartZ=0 EndX=-22.5736 EndY=70.7107 EndZ=0
    g3: LineSegment StartX=-22.5736 StartY=70.7107 StartZ=0 EndX=0 EndY=48.1371 EndZ=0
    g4: LineSegment StartX=0 StartY=48.1371 StartZ=0 EndX=0 EndY=0 EndZ=0
  constraints (14):
    c: Coincident(g-1,g0)
    c: Horizontal(g0)
    c: Coincident(g0,g1)
    c: Coincident(g1,g2)
    c: Coincident(g2,g3)
    c: PointOnObject(g3,g-2)
    c: Coincident(g3,g4)
    c: Coincident(g4,g0)
    c: DistanceX(g0,g0) = 65
    c: Angle(g0,g1) = 2.35619
    c: Distance(g1) = 20
    c: Angle(g1,g2) = 1.5708
    c: Distance(g2) = 80
    c: Angle(g2,g3) = 1.5708
FEATURE [PartDesign::Pad] Pad
  AllowMultiFace = false
  Direction = (1,1,1)
  Length = 35
  Length2 = 100
  Placement = pos=(0,0,0) rot=(0.57735,0.57735,0.57735;2.0944rad)
  Profile = -> Sketch
  Reversed = true
  Type = 0
  expr: Length = <<sp>>.largeurModuleBase
FEATURE [PartDesign::Plane] DatumPlane
  AttachmentOffset = pos=(71,0,0) rot=(0,-1,0;0.785398rad)
  Length = 98.6412
  MapMode = 5
  Placement = pos=(-7.9e-15,8e-15,71) rot=(0.678598,0.678598,0.281085;3.68962rad)
  ResizeMode = 0
  Support = -> [Pad]
  Width = 63.0813
FEATURE [PartDesign::Body] Body  label="Base"
  Group = -> [Sketch,Pad,DatumPlane]
  Origin = -> Origin001
  Tip = -> Pad
COMPONENT P3 — recipe-attached ("tigeLaiton001", modeled in this document).
Construction recipe (the document's own serialized feature program — sketch geometry with constraints, then the solid features built on it; lengths are millimeters unless a unit is written):

FEATURE [PartDesign::Plane] DatumPlane012  label="planBaseTige"
  AttachmentOffset = pos=(0,0,-5.18) rot=(0,0,1;0rad)
  Length = 60
  MapMode = 5
  Placement = pos=(-5.18,1.2e-15,-1.2e-15) rot=(0.57735,0.57735,0.57735;2.0944rad)
  ResizeMode = 0
  Support = -> [YZ_Plane012]
  Width = 60
  expr: .AttachmentOffset.Base.z = -<<tige>>.planBaseTigeposX
FEATURE [Sketcher::SketchObject] Sketch032  label="sk_tiges"
  FullyConstrained = true
  MapMode = 5
  Placement = pos=(-5.18,1.2e-15,-1.2e-15) rot=(0.57735,0.57735,0.57735;2.0944rad)
  Support = -> [DatumPlane012]
  expr: Constraints[0] = <<tige>>.tigeDiam
  expr: Constraints[1] = <<tige>>.tigePosY
  expr: Constraints[2] = <<tige>>.tigePosX
  sketch-geometry (1):
    g0: Circle CenterX=-14 CenterY=14.3 CenterZ=0 NormalX=0 NormalY=0 NormalZ=1 AngleXU=0 Radius=1.25
  constraints (3):
    c: Diameter(g0) = 2.5
    c: DistanceY(g-1,g0) = 14.3
    c: DistanceX(g0,g-1) = 14
FEATURE [PartDesign::Pad] Pad017  label="tigeBasse"
  AllowMultiFace = false
  Direction = (1,1,1)
  Length = 18.62
  Length2 = 100
  Placement = pos=(-5.18,1e-15,-1e-15) rot=(0.57735,0.57735,0.57735;2.0944rad)
  Profile = -> Sketch032
  Reversed = true
  Type = 0
  expr: Length = <<tige>>.tigeLong
FEATURE [PartDesign::Body] Body007  label="tigeLaiton"
  Group = -> [DatumPlane012,Sketch032,Pad017]
  Origin = -> Origin016
  Tip = -> Pad017
FEATURE [PartDesign::Plane] DatumPlane013  label="planTige2"
  AttachmentOffset = pos=(0,0,-5.18) rot=(0,0,1;0rad)
  Length = 60
  MapMode = 5
  Placement = pos=(-5.18,1.2e-15,-1.2e-15) rot=(0.57735,0.57735,0.57735;2.0944rad)
  ResizeMode = 0
  Support = -> [YZ_Plane014]
  Width = 60
  expr: .AttachmentOffset.Base.z = -<<tige>>.planBaseTigeposX
FEATURE [Sketcher::SketchObject] Sketch033  label="sk_tige2"
  FullyConstrained = true
  MapMode = 5
  Placement = pos=(-5.18,1.2e-15,-1.2e-15) rot=(0.57735,0.57735,0.57735;2.0944rad)
  Support = -> [DatumPlane013]
  expr: Constraints[0] = <<tige>>.tigeDiam
  expr: Constraints[1] = <<tige>>.tigePosX
  expr: Constraints[2] = <<tige>>.tigePosY + <<tige>>.xtEcartBroches
  sketch-geometry (1):
    g0: Circle CenterX=-14 CenterY=21.86 CenterZ=0 NormalX=0 NormalY=0 NormalZ=1 AngleXU=0 Radius=1.25
  constraints (3):
    c: Diameter(g0) = 2.5
    c: DistanceX(g0,g-1) = 14
    c: DistanceY(g-1,g0) = 21.86
FEATURE [PartDesign::Pad] Pad018
  AllowMultiFace = false
  Direction = (1,1,1)
  Length = 18.62
  Length2 = 100
  Placement = pos=(-5.18,1e-15,-1e-15) rot=(0.57735,0.57735,0.57735;2.0944rad)
  Profile = -> Sketch033
  Reversed = true
  Type = 0
  expr: Length = <<tige>>.tigeLong
FEATURE [PartDesign::Body] Body008  label="tige2"
  Group = -> [DatumPlane013,Sketch033,Pad018]
  Origin = -> Origin018
  Tip = -> Pad018
COMPONENT P4 — geometry summary ("xtVisInsertFix"; no construction recipe available for this part):
  bounding box: 20.2 x 17.7 x 16.6 mm
  tessellated surface: 21,972 triangles
  volume: 1306 mm^3 (22% of its bounding box)
COMPONENT P5 — geometry summary ("xtVisInertMob"; no construction recipe available for this part):
  bounding box: 20.5 x 17.8 x 16.5 mm
  tessellated surface: 31,892 triangles
  volume: 1060 mm^3 (18% of its bounding box)
COMPONENT P6 — recipe-attached ("visInsertFavFix", modeled in this document).
Construction recipe (the document's own serialized feature program — sketch geometry with constraints, then the solid features built on it; lengths are millimeters unless a unit is written):

FEATURE [Sketcher::SketchObject] Sketch034  label="Sketch"
  FullyConstrained = false
  MapMode = 5
  Support = -> [XY_Plane015]
  sketch-geometry (1):
    g0: Circle CenterX=0 CenterY=0 CenterZ=0 NormalX=0 NormalY=0 NormalZ=1 AngleXU=0 Radius=2.75
  constraints (2):
    c: Coincident(g0,g-1)
    c: Diameter(g0) = 5.5
FEATURE [PartDesign::Pad] Pad019  label="tete"
  AllowMultiFace = false
  Direction = (1,1,1)
  Length = 3
  Length2 = 100
  Profile = -> Sketch034
  Type = 0
FEATURE [Sketcher::SketchObject] Sketch001
  FullyConstrained = false
  MapMode = 5
  Placement = pos=(0,0,0) rot=(1,0,0;3.14159rad)
  Support = -> [Pad019]
  sketch-geometry (1):
    g0: Circle CenterX=0 CenterY=0 CenterZ=0 NormalX=0 NormalY=0 NormalZ=1 AngleXU=0 Radius=1.5
  constraints (2):
    c: Coincident(g0,g-1)
    c: Diameter(g0) = 3
FEATURE [PartDesign::Pad] Pad020  label="corps"
  AllowMultiFace = false
  BaseFeature = -> Pad019
  Direction = (1,1,1)
  Length = 6
  Length2 = 100
  Profile = -> Sketch001
  Type = 0
FEATURE [PartDesign::Plane] DatumPlane014
  AttachmentOffset = pos=(0,0,3) rot=(0,0,1;0rad)
  Length = 60
  MapMode = 5
  Placement = pos=(0,0,3) rot=(0,0,1;0rad)
  ResizeMode = 0
  Support = -> [XY_Plane015]
  Width = 60
FEATURE [Sketcher::SketchObject] Sketch035  label="Sketch002"
  FullyConstrained = false
  MapMode = 5
  Placement = pos=(0,0,3) rot=(0,0,1;0rad)
  Support = -> [DatumPlane014]
  sketch-geometry (7):
    g0: LineSegment StartX=0.721688 StartY=-1.25 StartZ=0 EndX=1.44338 EndY=1.0119e-12 EndZ=0
    g1: LineSegment StartX=1.44338 StartY=1.0119e-12 StartZ=0 EndX=0.721688 EndY=1.25 EndZ=0
    g2: LineSegment StartX=0.721688 StartY=1.25 StartZ=0 EndX=-0.721688 EndY=1.25 EndZ=0
    g3: LineSegment StartX=-0.721688 StartY=1.25 StartZ=0 EndX=-1.44338 EndY=8.689e-13 EndZ=0
    g4: LineSegment StartX=-1.44338 StartY=8.689e-13 StartZ=0 EndX=-0.721688 EndY=-1.25 EndZ=0
    g5: LineSegment StartX=-0.721688 StartY=-1.25 StartZ=0 EndX=0.721688 EndY=-1.25 EndZ=0
    g6: Circle CenterX=0 CenterY=0 CenterZ=0 NormalX=0 NormalY=0 NormalZ=1 AngleXU=0 Radius=1.44338
  constraints (16):
    c: Coincident(g0,g1)
    c: Coincident(g1,g2)
    c: Coincident(g2,g3)
    c: Coincident(g3,g4)
    c: Coincident(g4,g5)
    c: Coincident(g5,g0)
    c: Equal(g0, g1-g5) x5
    c: PointOnObject(g0,g6)
    c: PointOnObject(g1,g6)
    c: PointOnObject(g2,g6)
    c: PointOnObject(g3,g6)
    c: PointOnObject(g4,g6)
    c: PointOnObject(g5,g6)
    c: Coincident(g6,g-1)
    c: Horizontal(g2)
    c: DistanceY(g0,g1) = 2.5
FEATURE [PartDesign::Pocket] Pocket016  label="emprunte"
  AllowMultiFace = false
  BaseFeature = -> Pad020
  Direction = (1,1,1)
  Length = 4
  Length2 = 100
  Profile = -> Sketch035
  Type = 0
FEATURE [PartDesign::Body] Body009  label="visTHCM3x6_FAV001"
  Group = -> [Sketch034,Pad019,Sketch001,Pad020,DatumPlane014,Sketch035,Pocket016]
  Origin = -> Origin019
  Placement = pos=(-6.5,-61.8718,6.01041) rot=(1,0,0;3.92699rad)
  Tip = -> Pocket016
COMPONENT P7 — recipe-attached ("visInserFavMob", modeled in this document).
Construction recipe (the document's own serialized feature program — sketch geometry with constraints, then the solid features built on it; lengths are millimeters unless a unit is written):

FEATURE [Sketcher::SketchObject] Sketch036
  FullyConstrained = false
  MapMode = 5
  Support = -> [XY_Plane016]
  sketch-geometry (1):
    g0: Circle CenterX=0 CenterY=0 CenterZ=0 NormalX=0 NormalY=0 NormalZ=1 AngleXU=0 Radius=2.75
  constraints (2):
    c: Coincident(g0,g-1)
    c: Diameter(g0) = 5.5
FEATURE [PartDesign::Pad] Pad021  label="tete001"
  AllowMultiFace = false
  Direction = (1,1,1)
  Length = 3
  Length2 = 100
  Profile = -> Sketch036
  Type = 0
FEATURE [Sketcher::SketchObject] Sketch037
  FullyConstrained = false
  MapMode = 5
  Placement = pos=(0,0,0) rot=(1,0,0;3.14159rad)
  Support = -> [Pad021]
  sketch-geometry (1):
    g0: Circle CenterX=0 CenterY=0 CenterZ=0 NormalX=0 NormalY=0 NormalZ=1 AngleXU=0 Radius=1.5
  constraints (2):
    c: Coincident(g0,g-1)
    c: Diameter(g0) = 3
FEATURE [PartDesign::Pad] Pad022  label="corps001"
  AllowMultiFace = false
  BaseFeature = -> Pad021
  Direction = (1,1,1)
  Length = 6
  Length2 = 100
  Profile = -> Sketch037
  Type = 0
FEATURE [PartDesign::Plane] DatumPlane015
  AttachmentOffset = pos=(0,0,3) rot=(0,0,1;0rad)
  Length = 60
  MapMode = 5
  Placement = pos=(0,0,3) rot=(0,0,1;0rad)
  ResizeMode = 0
  Support = -> [XY_Plane016]
  Width = 60
FEATURE [Sketcher::SketchObject] Sketch038
  FullyConstrained = false
  MapMode = 5
  Placement = pos=(0,0,3) rot=(0,0,1;0rad)
  Support = -> [DatumPlane015]
  sketch-geometry (7):
    g0: LineSegment StartX=0.721688 StartY=-1.25 StartZ=0 EndX=1.44338 EndY=1.0119e-12 EndZ=0
    g1: LineSegment StartX=1.44338 StartY=1.0119e-12 StartZ=0 EndX=0.721688 EndY=1.25 EndZ=0
    g2: LineSegment StartX=0.721688 StartY=1.25 StartZ=0 EndX=-0.721688 EndY=1.25 EndZ=0
    g3: LineSegment StartX=-0.721688 StartY=1.25 StartZ=0 EndX=-1.44338 EndY=8.689e-13 EndZ=0
    g4: LineSegment StartX=-1.44338 StartY=8.689e-13 StartZ=0 EndX=-0.721688 EndY=-1.25 EndZ=0
    g5: LineSegment StartX=-0.721688 StartY=-1.25 StartZ=0 EndX=0.721688 EndY=-1.25 EndZ=0
    g6: Circle CenterX=0 CenterY=0 CenterZ=0 NormalX=0 NormalY=0 NormalZ=1 AngleXU=0 Radius=1.44338
  constraints (16):
    c: Coincident(g0,g1)
    c: Coincident(g1,g2)
    c: Coincident(g2,g3)
    c: Coincident(g3,g4)
    c: Coincident(g4,g5)
    c: Coincident(g5,g0)
    c: Equal(g0, g1-g5) x5
    c: PointOnObject(g0,g6)
    c: PointOnObject(g1,g6)
    c: PointOnObject(g2,g6)
    c: PointOnObject(g3,g6)
    c: PointOnObject(g4,g6)
    c: PointOnObject(g5,g6)
    c: Coincident(g6,g-1)
    c: Horizontal(g2)
    c: DistanceY(g0,g1) = 2.5
FEATURE [PartDesign::Pocket] Pocket017  label="emprunte001"
  AllowMultiFace = false
  BaseFeature = -> Pad022
  Direction = (1,1,1)
  Length = 4
  Length2 = 100
  Profile = -> Sketch038
  Type = 0
FEATURE [PartDesign::Body] Body010  label="visTHCM3x6_FAV002"
  Group = -> [Sketch036,Pad021,Sketch037,Pad022,DatumPlane015,Sketch038,Pocket017]
  Origin = -> Origin020
  Placement = pos=(-28.5,-61.8718,6.01041) rot=(1,0,0;3.92699rad)
  Tip = -> Pocket017
PROVENANCE & LICENSES
A FreeCAD (.FCStd) document from a public repository crawl; recipes are the document's own serialized feature recipes (and, for linked parts, companion documents' recipes).
License: as declared in the source repository (recorded in the dataset sidecar).
